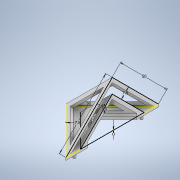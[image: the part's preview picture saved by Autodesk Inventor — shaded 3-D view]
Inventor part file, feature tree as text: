
AUTODESK INVENTOR PART (.ipt)
format: ipt  version: 2020 (Build 240168000, 168)  size: 235,008 bytes
history: native  units: mm
features: extrude x9, sketch x9, plane x4, split x2, shell x2, draft x1
ambient origin geometry x8: Origin, YZ Plane, XZ Plane, XY Plane, X Axis, Y Axis, Z Axis, Center Point
bodies: Solid1 (feature_tree), Solid4 (feature_tree)
feature tree (27):
  extrude  "Extrusion1"  Depth=2.0mm TaperAngle=0.0deg
  sketch  "Sketch3"  dims[d1=50.0mm d2=2.0mm d3=0.0mm]
  sketch  "Sketch12"  dims[d41=70.71mm d42=50.0mm d43=50.0mm]
  plane  "Work Plane5"
  plane  "Work Plane6"
  extrude  "Extrusion10"  Depth=50.0mm
  split  "Split3"
  shell  "Shell3"  Thickness=50.0mm
  sketch  "Sketch13"  dims[d44=10.0mm d45=0.0mm d46=0.0mm]
  extrude  "Extrusion17"  TaperAngle=0.0deg  [1 undecoded]
  draft  "FaceDraft2"
  plane  "Work Plane9"
  plane  "Work Plane10"
  extrude  "Extrusion18"  Depth=2.0mm
  split  "Split5"
  shell  "Shell5"  Thickness=2.0mm
  extrude  "Extrusion19"  Depth=7.8mm
  extrude  "Extrusion20"  Depth=2.0mm
  extrude  "Extrusion21"  Depth=5.0mm TaperAngle=0.0deg
  extrude  "Extrusion22"  Depth=10.0mm TaperAngle=0.0deg
  extrude  "Extrusion23"  Depth=10.0mm TaperAngle=0.0deg
  sketch  "Sketch19"  dims[d47=7.8mm d48=7.8mm d49=2.0mm]
  sketch  "Sketch20"  dims[d52=7.8mm d53=7.8mm]
  sketch  "Sketch21"  dims[d79=2.0mm d80=2.0mm]
  sketch  "Sketch22"  dims[d81=2.0mm d82=5.0mm d83=0.0mm]
  sketch  "Sketch23"  dims[d84=1.745329mm d85=10.0mm d86=0.0mm]
  sketch  "Sketch24"  dims[d87=2.0mm d88=10.0mm d89=0.0mm d90=4.0mm d91=4.0mm d92=4.0mm d93=2.0mm d94=0.0mm d95=4.0mm d96=4.0mm d97=4.0mm d98=2.0mm d99=0.0mm d100=4.0mm d101=4.0mm d102=4.0mm d103=2.0mm d104=0.0mm d105=4.0mm d106=4.0mm d107=4.0mm d108=2.0mm d109=0.0mm]
note: 1 required parameter value undecoded (feature->parameter linkage not recoverable at this tier; creation-order binding heuristic only, values carry confidence <= 0.55)
